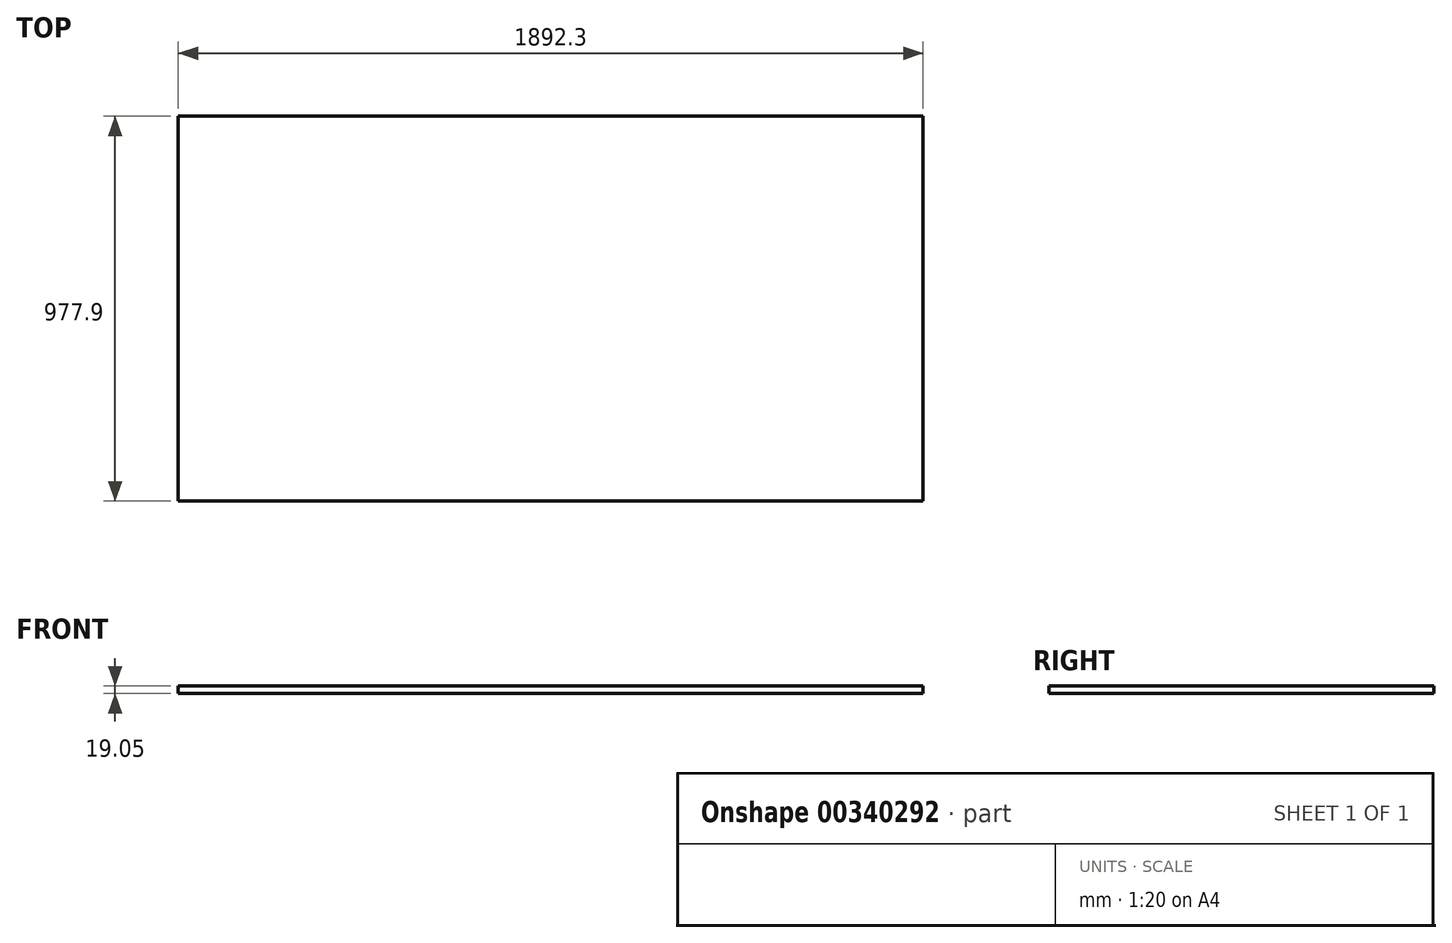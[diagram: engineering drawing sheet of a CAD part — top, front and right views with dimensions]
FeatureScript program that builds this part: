
annotation { "Feature Type Name" : "Feature", "Feature Type Description" : "" }
export const myFeature = defineFeature(function(context is Context, id is Id, definition is map)
    precondition{}
    {
        {
            var Q0;
            Q0=qCreatedBy(makeId("Top.planeOp"),FACE);
            var sketch = newSketch(context, id + "F0", { "sketchPlane" : qUnion([Q0])});
            skLineSegment(sketch, "E0.bottom", {"start": v(946.15, -488.95) * mm, "end": v(-946.15, -488.95) * mm});
            skLineSegment(sketch, "E0.top", {"start": v(946.15, 488.95) * mm, "end": v(-946.15, 488.95) * mm});
            skLineSegment(sketch, "E0.left", {"start": v(946.15, -488.95) * mm, "end": v(946.15, 488.95) * mm});
            skLineSegment(sketch, "E0.right", {"start": v(-946.15, -488.95) * mm, "end": v(-946.15, 488.95) * mm});
            skPoint(sketch, "E0.middle", {"position": v(0, 0) * mm});
            skSolve(sketch);
        }
        {
            var Q0;
            Q0 = qSketchRegion(id + "F0", true);
            extrude(context, id + "F1", {"entities" : qUnion([Q0]), "depth" : 19.05 * mm});
        }
    });
